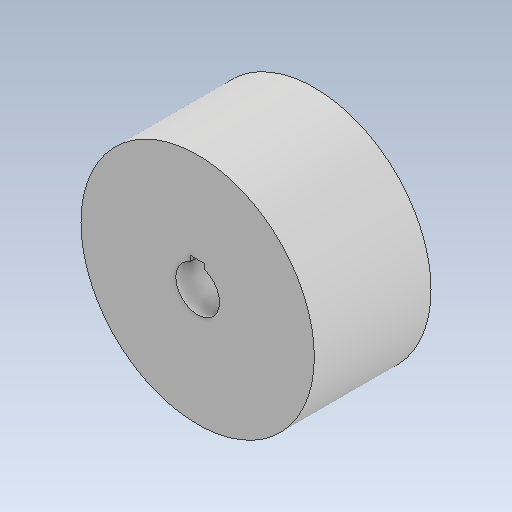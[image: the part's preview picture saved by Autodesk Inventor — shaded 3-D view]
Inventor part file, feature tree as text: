
AUTODESK INVENTOR PART (.ipt)
format: ipt  version: 2021 (Build 250183000, 183)  size: 104,448 bytes
history: native  units: in
note: dims shown in document units (in); Inventor stores cm internally (conversion verified against a paired STEP export)
features: other x3, extrude x1, sketch x1, reference x1
ambient origin geometry x8: Origin, YZ Plane, XZ Plane, XY Plane, X Axis, Y Axis, Z Axis, Center Point
bodies: Solid1 (feature_tree)
feature tree (6):
  extrude  "Extrusion1"  Depth=1.0in TaperAngle=0.0deg
  sketch  "Sketch1"  dims[d0=2.0in d1=1.0in d2=0.0in]
  reference  "Reference1"
  parser-record x1  (decoder bookkeeping rows leaked as tree rows — omitted from the tree; the rows remain in map.json)
  other  "ForkMount.iam"
  other  "12x3_8-keyedDriveShaft:1"
note: 1 file-system path scrubbed to <path> (originals preserved in map.json)
